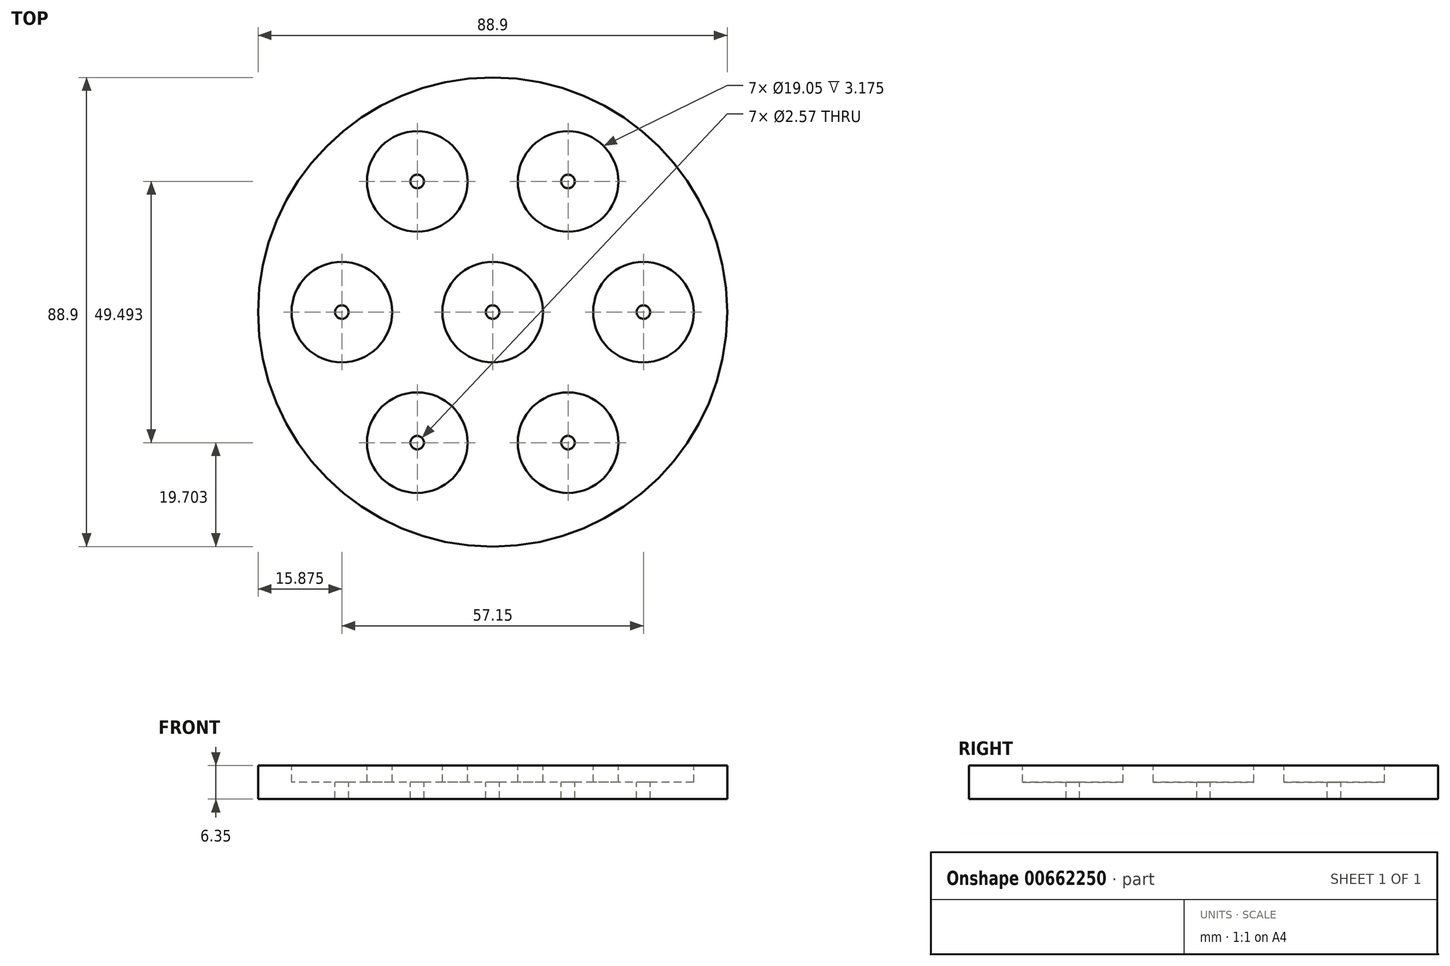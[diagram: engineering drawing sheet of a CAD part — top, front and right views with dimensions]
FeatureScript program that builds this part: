
annotation { "Feature Type Name" : "Feature", "Feature Type Description" : "" }
export const myFeature = defineFeature(function(context is Context, id is Id, definition is map)
    precondition{}
    {
        {
            var Q0;
            Q0=qCreatedBy(makeId("Top.planeOp"),FACE);
            var sketch = newSketch(context, id + "F0", { "sketchPlane" : qUnion([Q0])});
            skCircle(sketch, "E0", {"center": v(0, 0) * mm, "radius": 44.45 * mm});
            skSolve(sketch);
        }
        {
            var Q0;
            Q0 = qSketchRegion(id + "F0", true);
            extrude(context, id + "F1", {"entities" : qUnion([Q0]), "depth" : 6.35 * mm, "offsetDistance" : 25.4 * mm});
        }
        {
            var Q0;
            Q0=makeQuery(id+"F1.opExtrude","CAP_FACE",FACE,{"disambiguationData":[OSD([sQuery(id+"F0.wireOp",EDGE,"E0")])],"isStart":false});
            var sketch = newSketch(context, id + "F2", { "sketchPlane" : qUnion([Q0])});
            skCircle(sketch, "E1", {"center": v(0, 0) * mm, "radius": 9.53 * mm});
            skCircle(sketch, "E2", {"center": v(28.58, 0) * mm, "radius": 9.53 * mm});
            skCircle(sketch, "E3.1.0", {"center": v(14.29, 24.75) * mm, "radius": 9.53 * mm});
            skCircle(sketch, "E3.2.0", {"center": v(-14.29, 24.75) * mm, "radius": 9.53 * mm});
            skCircle(sketch, "E3.3.0", {"center": v(-28.58, 0) * mm, "radius": 9.53 * mm});
            skCircle(sketch, "E3.4.0", {"center": v(-14.29, -24.75) * mm, "radius": 9.53 * mm});
            skCircle(sketch, "E3.5.0", {"center": v(14.29, -24.75) * mm, "radius": 9.53 * mm});
            skSolve(sketch);
        }
        {
            var Q0;
            Q0=makeQuery(id+"F2.imprint","IMPRINT",FACE,{"disambiguationData":[TD([[makeQuery(id+"F2.imprint","IMPRINT",EDGE,{"derivedFrom":sQuery(id+"F2.wireOp",EDGE,"E3.3.0")}),1.0]])]});
            var Q1;
            Q1=makeQuery(id+"F2.imprint","IMPRINT",FACE,{"disambiguationData":[TD([[makeQuery(id+"F2.imprint","IMPRINT",EDGE,{"derivedFrom":sQuery(id+"F2.wireOp",EDGE,"E3.2.0")}),1.0]])]});
            var Q2;
            Q2=makeQuery(id+"F2.imprint","IMPRINT",FACE,{"disambiguationData":[TD([[makeQuery(id+"F2.imprint","IMPRINT",EDGE,{"derivedFrom":sQuery(id+"F2.wireOp",EDGE,"E3.1.0")}),1.0]])]});
            var Q3;
            Q3=makeQuery(id+"F2.imprint","IMPRINT",FACE,{"disambiguationData":[TD([[makeQuery(id+"F2.imprint","IMPRINT",EDGE,{"derivedFrom":sQuery(id+"F2.wireOp",EDGE,"E2")}),1.0]])]});
            var Q4;
            Q4=makeQuery(id+"F2.imprint","IMPRINT",FACE,{"disambiguationData":[TD([[makeQuery(id+"F2.imprint","IMPRINT",EDGE,{"derivedFrom":sQuery(id+"F2.wireOp",EDGE,"E1")}),1.0]])]});
            var Q5;
            Q5=makeQuery(id+"F2.imprint","IMPRINT",FACE,{"disambiguationData":[TD([[makeQuery(id+"F2.imprint","IMPRINT",EDGE,{"derivedFrom":sQuery(id+"F2.wireOp",EDGE,"E3.5.0")}),1.0]])]});
            var Q6;
            Q6=makeQuery(id+"F2.imprint","IMPRINT",FACE,{"disambiguationData":[TD([[makeQuery(id+"F2.imprint","IMPRINT",EDGE,{"derivedFrom":sQuery(id+"F2.wireOp",EDGE,"E3.4.0")}),1.0]])]});
            extrude(context, id + "F3", {"entities" : qUnion([Q0, Q1, Q2, Q3, Q4, Q5, Q6]), "operationType" : NewBodyOperationType.REMOVE, "oppositeDirection" : true, "depth" : 3.17 * mm, "offsetDistance" : 25.4 * mm});
        }
        {
            var Q0;
            Q0=makeQuery(id+"F1.opExtrude","CAP_FACE",FACE,{"disambiguationData":[OSD([sQuery(id+"F0.wireOp",EDGE,"E0")])],"isStart":false});
            var sketch = newSketch(context, id + "F4", { "sketchPlane" : qUnion([Q0])});
            skCircle(sketch, "E4", {"center": v(0, 0) * mm, "radius": 1.28 * mm});
            skCircle(sketch, "E5", {"center": v(28.58, 0) * mm, "radius": 1.28 * mm});
            skCircle(sketch, "E6.1.0", {"center": v(14.29, 24.75) * mm, "radius": 1.28 * mm});
            skCircle(sketch, "E6.2.0", {"center": v(-14.29, 24.75) * mm, "radius": 1.28 * mm});
            skCircle(sketch, "E6.3.0", {"center": v(-28.58, 0) * mm, "radius": 1.28 * mm});
            skCircle(sketch, "E6.4.0", {"center": v(-14.29, -24.75) * mm, "radius": 1.28 * mm});
            skCircle(sketch, "E6.5.0", {"center": v(14.29, -24.75) * mm, "radius": 1.28 * mm});
            skSolve(sketch);
        }
        {
            var Q0;
            Q0=makeQuery(id+"F4.imprint","IMPRINT",FACE,{"disambiguationData":[TD([[makeQuery(id+"F4.imprint","IMPRINT",EDGE,{"derivedFrom":sQuery(id+"F4.wireOp",EDGE,"E5")}),1.0]])]});
            var Q1;
            Q1=makeQuery(id+"F4.imprint","IMPRINT",FACE,{"disambiguationData":[TD([[makeQuery(id+"F4.imprint","IMPRINT",EDGE,{"derivedFrom":sQuery(id+"F4.wireOp",EDGE,"E4")}),1.0]])]});
            var Q2;
            Q2=makeQuery(id+"F4.imprint","IMPRINT",FACE,{"disambiguationData":[TD([[makeQuery(id+"F4.imprint","IMPRINT",EDGE,{"derivedFrom":sQuery(id+"F4.wireOp",EDGE,"E6.2.0")}),1.0]])]});
            var Q3;
            Q3=makeQuery(id+"F4.imprint","IMPRINT",FACE,{"disambiguationData":[TD([[makeQuery(id+"F4.imprint","IMPRINT",EDGE,{"derivedFrom":sQuery(id+"F4.wireOp",EDGE,"E6.1.0")}),1.0]])]});
            var Q4;
            Q4=makeQuery(id+"F4.imprint","IMPRINT",FACE,{"disambiguationData":[TD([[makeQuery(id+"F4.imprint","IMPRINT",EDGE,{"derivedFrom":sQuery(id+"F4.wireOp",EDGE,"E6.3.0")}),1.0]])]});
            var Q5;
            Q5=makeQuery(id+"F4.imprint","IMPRINT",FACE,{"disambiguationData":[TD([[makeQuery(id+"F4.imprint","IMPRINT",EDGE,{"derivedFrom":sQuery(id+"F4.wireOp",EDGE,"E6.4.0")}),1.0]])]});
            var Q6;
            Q6=makeQuery(id+"F4.imprint","IMPRINT",FACE,{"disambiguationData":[TD([[makeQuery(id+"F4.imprint","IMPRINT",EDGE,{"derivedFrom":sQuery(id+"F4.wireOp",EDGE,"E6.5.0")}),1.0]])]});
            extrude(context, id + "F5", {"entities" : qUnion([Q0, Q1, Q2, Q3, Q4, Q5, Q6]), "operationType" : NewBodyOperationType.REMOVE, "oppositeDirection" : true, "depth" : 25.4 * mm, "offsetDistance" : 25.4 * mm});
        }
    });
